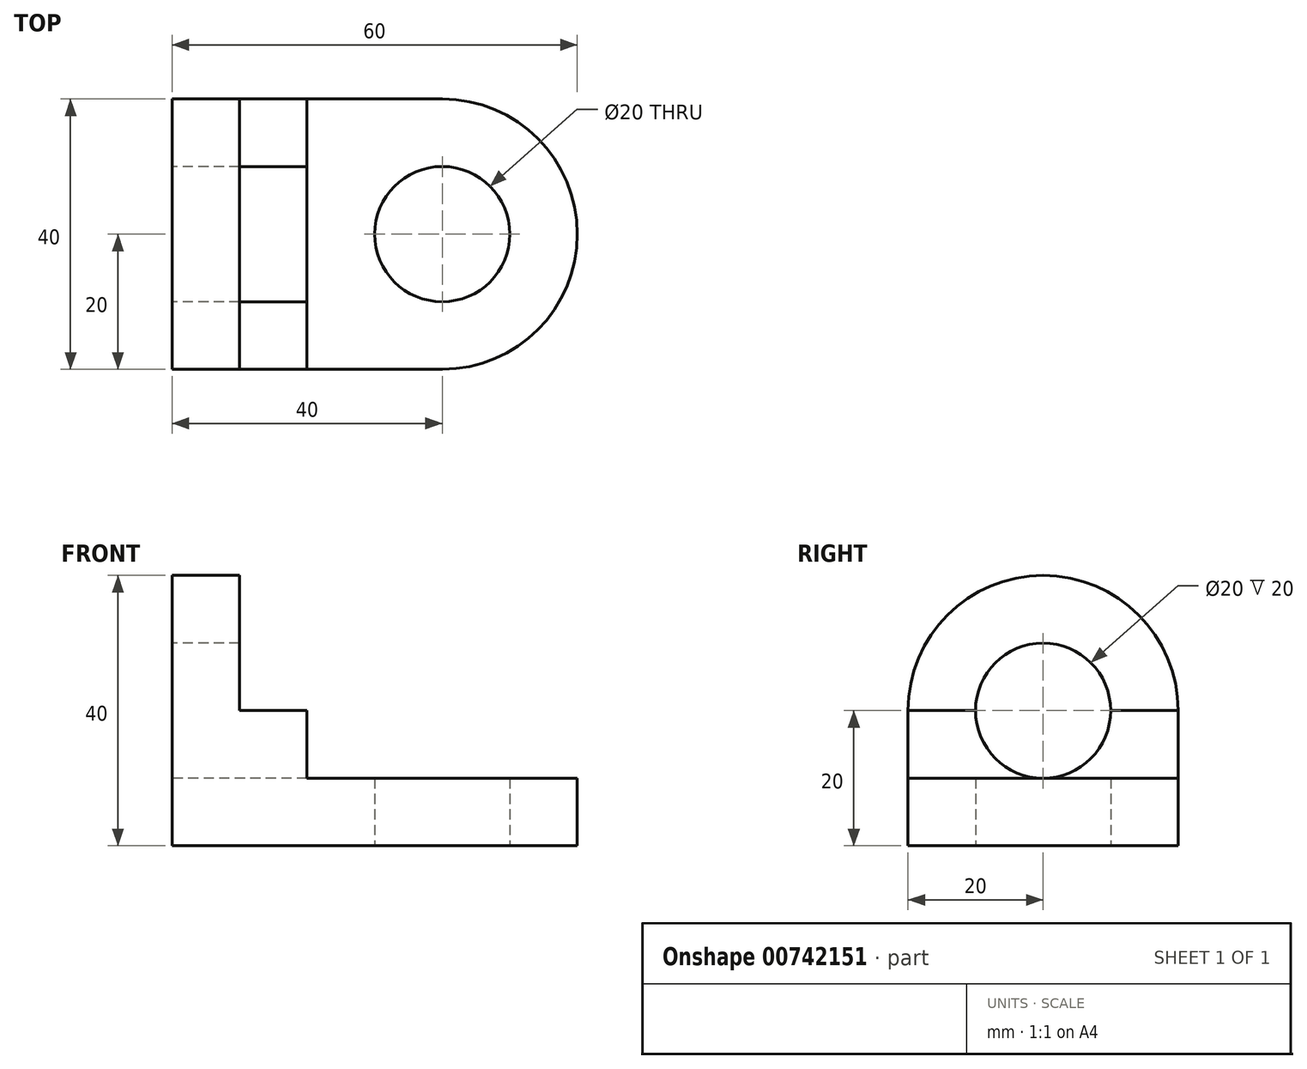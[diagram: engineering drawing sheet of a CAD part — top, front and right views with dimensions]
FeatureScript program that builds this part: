
annotation { "Feature Type Name" : "Feature", "Feature Type Description" : "" }
export const myFeature = defineFeature(function(context is Context, id is Id, definition is map)
    precondition{}
    {
        {
            var Q0;
            Q0=qCreatedBy(makeId("Front.planeOp"),FACE);
            var sketch = newSketch(context, id + "F0", { "sketchPlane" : qUnion([Q0])});
            skLineSegment(sketch, "E0.bottom", {"start": v(0, 0) * mm, "end": v(60, 0) * mm});
            skLineSegment(sketch, "E0.top", {"start": v(0, 10) * mm, "end": v(60, 10) * mm});
            skLineSegment(sketch, "E0.left", {"start": v(0, 0) * mm, "end": v(0, 10) * mm});
            skLineSegment(sketch, "E0.right", {"start": v(60, 0) * mm, "end": v(60, 10) * mm});
            skLineSegment(sketch, "E1.bottom", {"start": v(0, 10) * mm, "end": v(20, 10) * mm});
            skLineSegment(sketch, "E1.top", {"start": v(0, 20) * mm, "end": v(20, 20) * mm});
            skLineSegment(sketch, "E1.left", {"start": v(0, 10) * mm, "end": v(0, 20) * mm});
            skLineSegment(sketch, "E1.right", {"start": v(20, 10) * mm, "end": v(20, 20) * mm});
            skLineSegment(sketch, "E2.bottom", {"start": v(0, 20) * mm, "end": v(10, 20) * mm});
            skLineSegment(sketch, "E2.top", {"start": v(0, 40) * mm, "end": v(10, 40) * mm});
            skLineSegment(sketch, "E2.left", {"start": v(0, 20) * mm, "end": v(0, 40) * mm});
            skLineSegment(sketch, "E2.right", {"start": v(10, 20) * mm, "end": v(10, 40) * mm});
            skSolve(sketch);
        }
        {
            var Q0;
            Q0 = qSketchRegion(id + "F0", true);
            extrude(context, id + "F1", {"entities" : qUnion([Q0]), "depth" : 40 * mm, "offsetDistance" : 25.4 * mm});
        }
        {
            var Q0;
            Q0=qCreatedBy(makeId("Top.planeOp"),FACE);
            var sketch = newSketch(context, id + "F2", { "sketchPlane" : qUnion([Q0])});
            skLineSegment(sketch, "E3", {"start": v(0, 0) * mm, "end": v(60, 0) * mm});
            skLineSegment(sketch, "E4", {"start": v(0, 0) * mm, "end": v(30, 0) * mm});
            skLineSegment(sketch, "E5", {"start": v(0, 0) * mm, "end": v(0, -40) * mm});
            skLineSegment(sketch, "E6", {"start": v(0, 0) * mm, "end": v(0, -20) * mm});
            skLineSegment(sketch, "E7", {"start": v(0, 0) * mm, "end": v(20, 0) * mm});
            skLineSegment(sketch, "E8", {"start": v(20, 0) * mm, "end": v(40, 0) * mm});
            skCircle(sketch, "E9", {"center": v(40, -20) * mm, "radius": 10 * mm});
            skSolve(sketch);
        }
        {
            var Q0;
            Q0=makeQuery(id+"F2.imprint","IMPRINT",FACE,{"disambiguationData":[TD([[makeQuery(id+"F2.imprint","IMPRINT",EDGE,{"derivedFrom":sQuery(id+"F2.wireOp",EDGE,"E9")}),1.0]])]});
            extrude(context, id + "F3", {"entities" : qUnion([Q0]), "operationType" : NewBodyOperationType.REMOVE, "endBound" : BoundingType.THROUGH_ALL, "depth" : 28.9 * mm, "offsetDistance" : 25 * mm});
        }
        {
            var Q0;
            Q0=makeQuery(id+"F1.opExtrude","SWEPT_FACE",FACE,{"disambiguationData":[OSD([sQuery(id+"F0.wireOp",EDGE,"E0.left"),sQuery(id+"F0.wireOp",EDGE,"E1.left"),sQuery(id+"F0.wireOp",EDGE,"E2.left")])]});
            var sketch = newSketch(context, id + "F4", { "sketchPlane" : qUnion([Q0])});
            skLineSegment(sketch, "E10", {"start": v(40, 0) * mm, "end": v(0, 0) * mm});
            skLineSegment(sketch, "E11", {"start": v(0, 0) * mm, "end": v(20, 0) * mm});
            skLineSegment(sketch, "E12", {"start": v(20, 0) * mm, "end": v(20, 40) * mm});
            skLineSegment(sketch, "E13", {"start": v(20, 40) * mm, "end": v(20, 20) * mm});
            skCircle(sketch, "E14", {"center": v(20, 20) * mm, "radius": 10 * mm});
            skSolve(sketch);
        }
        {
            var Q0;
            Q0 = qSketchRegion(id + "F4", true);
            extrude(context, id + "F5", {"entities" : qUnion([Q0]), "operationType" : NewBodyOperationType.REMOVE, "endBound" : BoundingType.THROUGH_ALL, "oppositeDirection" : true, "depth" : 25 * mm, "offsetDistance" : 25 * mm});
        }
        {
            var Q0;
            Q0=makeQuery(id+"F1.opExtrude","SWEPT_FACE",FACE,{"disambiguationData":[OSD([sQuery(id+"F0.wireOp",EDGE,"E2.right")])]});
            var sketch = newSketch(context, id + "F6", { "sketchPlane" : qUnion([Q0])});
            skSolve(sketch);
        }
        {
            var Q0;
            Q0=makeQuery(id+"F1.opExtrude","CAP_EDGE",EDGE,{"disambiguationData":[OSD([sQuery(id+"F0.wireOp",EDGE,"E2.top")])],"isStart":false});
            var Q1;
            Q1=makeQuery(id+"F1.opExtrude","CAP_EDGE",EDGE,{"disambiguationData":[OSD([sQuery(id+"F0.wireOp",EDGE,"E2.top")])],"isStart":true});
            fillet(context, id + "F7", {"entities" : qUnion([Q0, Q1]), "radius" : 20 * mm, "tangentPropagation" : true, "allowEdgeOverflow" : false});
        }
        {
            var Q0;
            Q0=makeQuery(id+"F1.opExtrude","CAP_EDGE",EDGE,{"disambiguationData":[OSD([sQuery(id+"F0.wireOp",EDGE,"E0.right")])],"isStart":true});
            var Q1;
            Q1=makeQuery(id+"F1.opExtrude","CAP_EDGE",EDGE,{"disambiguationData":[OSD([sQuery(id+"F0.wireOp",EDGE,"E0.right")])],"isStart":false});
            fillet(context, id + "F8", {"entities" : qUnion([Q0, Q1]), "radius" : 20 * mm, "tangentPropagation" : true, "allowEdgeOverflow" : false});
        }
    });
